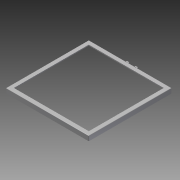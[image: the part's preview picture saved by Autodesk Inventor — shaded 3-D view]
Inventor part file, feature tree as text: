
AUTODESK INVENTOR PART (.ipt)
format: ipt  version: 2014 (Build 180170000, 170)  size: 195,584 bytes
history: native  units: in
note: dims shown in document units (in); Inventor stores cm internally (conversion verified against a paired STEP export)
features: extrude x6, sketch x6, fillet x3, mirror x3, thread x2
ambient origin geometry x8: Origin, YZ Plane, XZ Plane, XY Plane, X Axis, Y Axis, Z Axis, Center Point
bodies: Solid1 (feature_tree)
feature tree (20):
  extrude  "Extrusion1"  Depth=25.997in
  extrude  "Extrusion2"  Depth=0.0625in
  fillet  "Fillet1"  Radius=1.4375in
  extrude  "Extrusion3"  Depth=0.125in
  extrude  "Extrusion4"  Depth=0.375in
  fillet  "Fillet2"  Radius=0.75in
  fillet  "Fillet3"  Radius=0.75in
  mirror  "Mirror1"
  extrude  "Extrusion5"  Depth=0.375in
  thread  "Thread1"  [1 undecoded]
  mirror  "Mirror2"
  thread  "Thread2"  [1 undecoded]
  extrude  "Extrusion6"  Depth=0.0625in
  mirror  "Mirror3"
  sketch  "Sketch1"  dims[d0=25.997in d2=25.997in]
  sketch  "Sketch2"  dims[d3=0.0625in d4=0.0625in d5=1.4375in d6=0.0in]
  sketch  "Sketch3"  dims[d9=0.0625in d10=0.0in d11=0.125in]
  sketch  "Sketch4"  dims[d12=0.75in d14=0.375in d15=0.75in d17=0.75in d18=0.0in]
  sketch  "Sketch5"  dims[d19=0.25in d21=0.375in d22=0.375in d23=0.75in d24=0.0in]
  sketch  "Sketch6"  dims[d25=0.0625in d26=0.0625in d27=0.25in d28=0.3125in d29=0.3125in d30=0.75in d31=0.0in d32=1.0in d33=0.0in d34=1.0in d35=0.0in d36=0.25in d37=2.375in d38=0.75in d39=0.0in d142=-2.3125in d145=1.0in d146=1.25in d147=1.25in]
note: 2 required parameter values undecoded (feature->parameter linkage not recoverable at this tier; creation-order binding heuristic only, values carry confidence <= 0.55)
